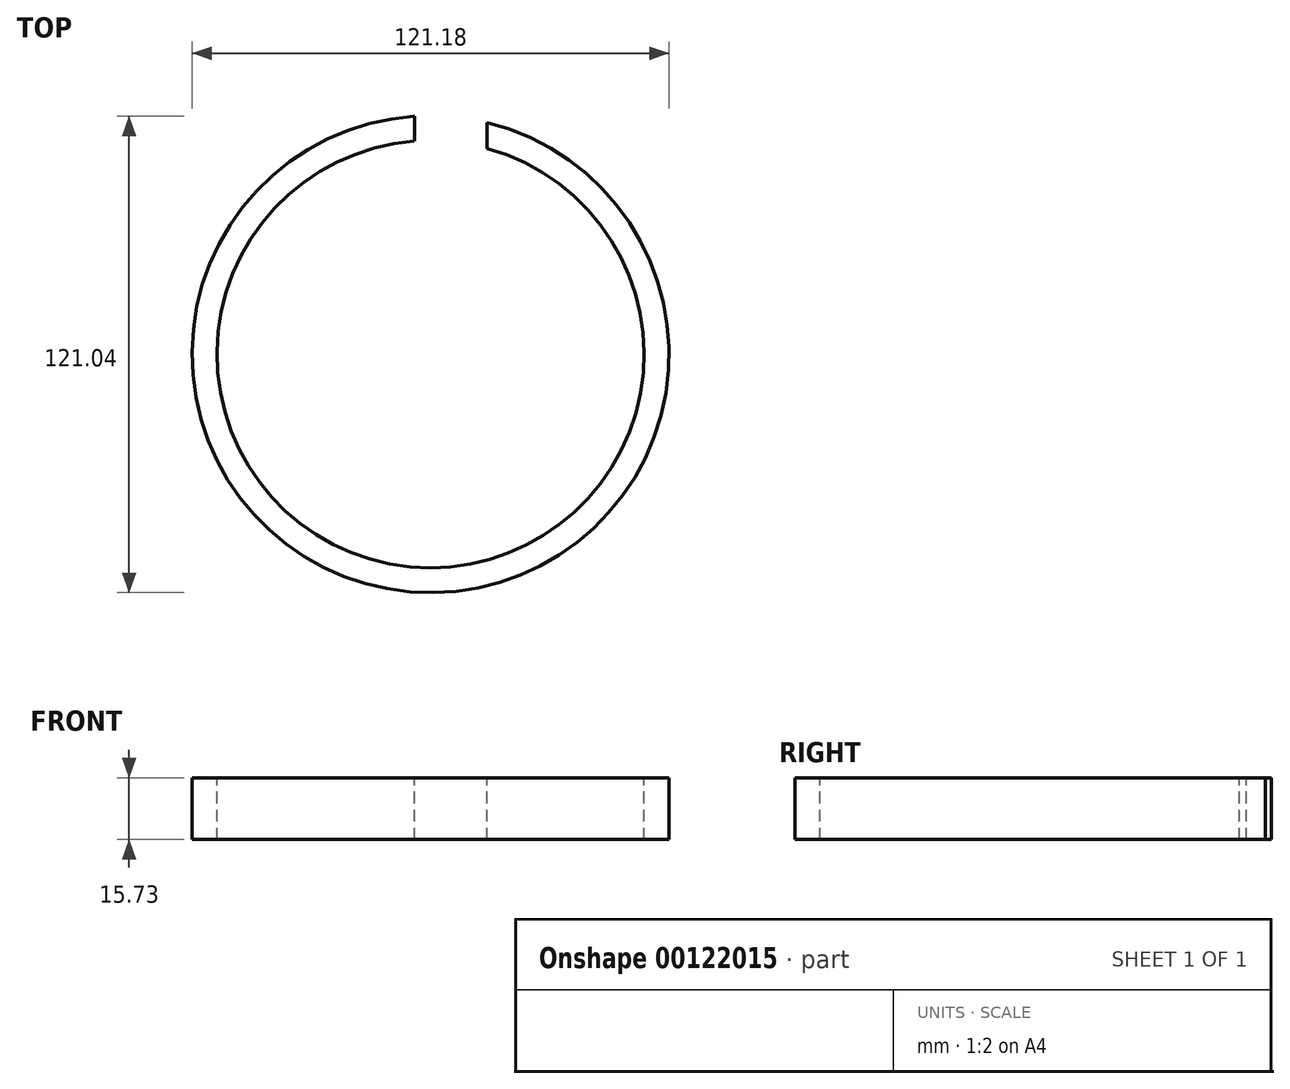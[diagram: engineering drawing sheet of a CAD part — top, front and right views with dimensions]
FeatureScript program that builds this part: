
annotation { "Feature Type Name" : "Feature", "Feature Type Description" : "" }
export const myFeature = defineFeature(function(context is Context, id is Id, definition is map)
    precondition{}
    {
        {
            var Q0;
            Q0=qCreatedBy(makeId("Front.planeOp"),FACE);
            var sketch = newSketch(context, id + "F0", { "sketchPlane" : qUnion([Q0])});
            skLineSegment(sketch, "E0.bottom", {"start": v(-28, 10.54) * mm, "end": v(-21.67, 10.54) * mm});
            skLineSegment(sketch, "E0.top", {"start": v(-28, -5.2) * mm, "end": v(-21.67, -5.2) * mm});
            skLineSegment(sketch, "E0.left", {"start": v(-28, 10.54) * mm, "end": v(-28, -5.2) * mm});
            skLineSegment(sketch, "E0.right", {"start": v(-21.67, 10.54) * mm, "end": v(-21.67, -5.2) * mm});
            skLineSegment(sketch, "E1", {"start": v(0, 10.54) * mm, "end": v(0, -4.72) * mm, "construction": true});
            skLineSegment(sketch, "E2", {"start": v(32.58, 10.54) * mm, "end": v(32.58, -5.69) * mm, "construction": true});
            skSolve(sketch);
        }
        {
            var Q0;
            Q0=makeQuery(id+"F0.imprint","IMPRINT",FACE,{"disambiguationData":[TD([[makeQuery(id+"F0.imprint","IMPRINT",EDGE,{"derivedFrom":sQuery(id+"F0.wireOp",EDGE,"E0.bottom")}),-1.0]])]});
            var Q1;
            Q1=sQuery(id+"F0.wireOp",EDGE,"E2");
            revolve(context, id + "F1", {"entities" : qUnion([Q0]), "axis" : qUnion([Q1]), "revolveType" : RevolveType.FULL});
        }
        {
            var Q0;
            Q0=qCreatedBy(makeId("Front.planeOp"),FACE);
            var sketch = newSketch(context, id + "F2", { "sketchPlane" : qUnion([Q0])});
            skLineSegment(sketch, "E3.bottom", {"start": v(28.46, 20.07) * mm, "end": v(46.98, 20.07) * mm});
            skLineSegment(sketch, "E3.top", {"start": v(28.46, -5.26) * mm, "end": v(46.98, -5.26) * mm});
            skLineSegment(sketch, "E3.left", {"start": v(28.46, 20.07) * mm, "end": v(28.46, -5.26) * mm});
            skLineSegment(sketch, "E3.right", {"start": v(46.98, 20.07) * mm, "end": v(46.98, -5.26) * mm});
            skSolve(sketch);
        }
        {
            var Q0;
            Q0=makeQuery(id+"F2.imprint","IMPRINT",FACE,{"disambiguationData":[TD([[makeQuery(id+"F2.imprint","IMPRINT",EDGE,{"derivedFrom":sQuery(id+"F2.wireOp",EDGE,"E3.bottom")}),-1.0]])]});
            extrude(context, id + "F3", {"entities" : qUnion([Q0]), "operationType" : NewBodyOperationType.REMOVE, "oppositeDirection" : true, "depth" : 177.8 * mm});
        }
    });
